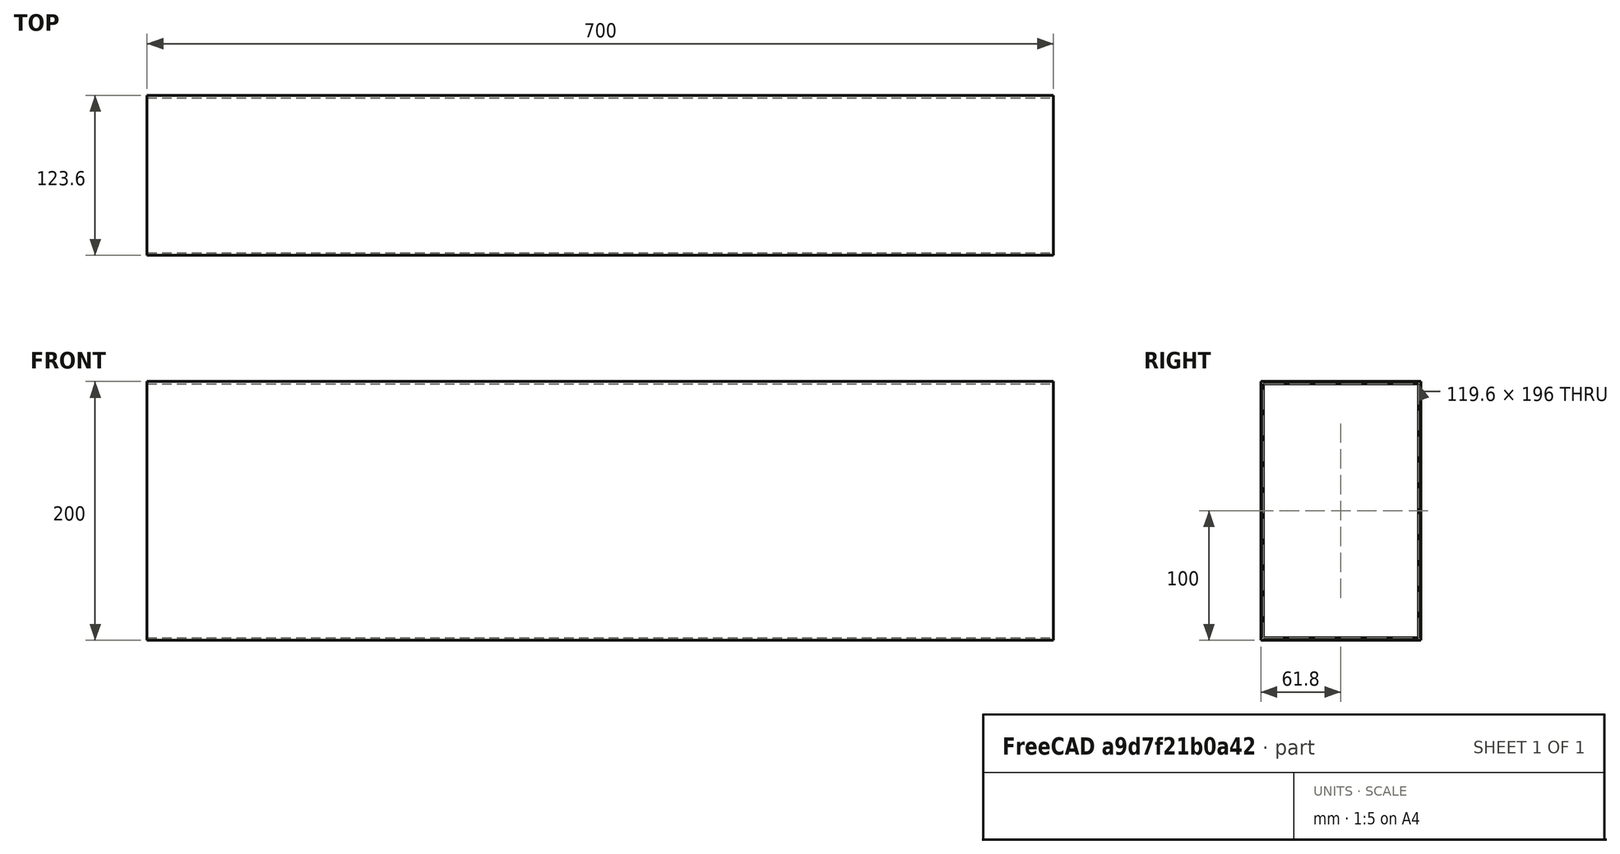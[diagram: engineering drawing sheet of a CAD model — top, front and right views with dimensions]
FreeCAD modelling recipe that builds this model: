
FCSTD DOCUMENT  (FreeCAD 0.20R29410 (Git))
Label: bigSling
License: All rights reserved
LicenseURL: http://en.wikipedia.org/wiki/All_rights_reserved
objects: PartDesign::Body×2, Sketcher::SketchObject×1, PartDesign::Pad×1
note: 5 computed .brp shape members not serialized (recipe doc carries the construction recipe); baked Part::Feature solids carry a one-line shape summary decoded from their .brp

FEATURE [PartDesign::Body] Body
  Origin = -> Origin
FEATURE [Sketcher::SketchObject] Sketch
  FullyConstrained = true
  MapMode = 5
  Placement = pos=(0,0,0) rot=(0.57735,0.57735,0.57735;2.0944rad)
  Support = -> [YZ_Plane001]
  sketch-geometry (8):
    g0: LineSegment StartX=0 StartY=0 StartZ=0 EndX=123.6 EndY=0 EndZ=0
    g1: LineSegment StartX=123.6 StartY=0 StartZ=0 EndX=123.6 EndY=-200 EndZ=0
    g2: LineSegment StartX=123.6 StartY=-200 StartZ=0 EndX=0 EndY=-200 EndZ=0
    g3: LineSegment StartX=0 StartY=-200 StartZ=0 EndX=0 EndY=0 EndZ=0
    g4: LineSegment StartX=2 StartY=-2 StartZ=0 EndX=121.6 EndY=-2 EndZ=0
    g5: LineSegment StartX=121.6 StartY=-2 StartZ=0 EndX=121.6 EndY=-198 EndZ=0
    g6: LineSegment StartX=121.6 StartY=-198 StartZ=0 EndX=2 EndY=-198 EndZ=0
    g7: LineSegment StartX=2 StartY=-198 StartZ=0 EndX=2 EndY=-2 EndZ=0
  constraints (23):
    c: Coincident(g0,g1)
    c: Coincident(g1,g2)
    c: Coincident(g2,g3)
    c: Coincident(g3,g0)
    c: Horizontal(g0)
    c: Horizontal(g2)
    c: Vertical(g1)
    c: Vertical(g3)
    c: Coincident(g0,g-1)
    c: Coincident(g4,g5)
    c: Coincident(g5,g6)
    c: Coincident(g6,g7)
    c: Coincident(g7,g4)
    c: Horizontal(g4)
    c: Horizontal(g6)
    c: Vertical(g5)
    c: Vertical(g7)
    c: DistanceY(g3,g3) = 200
    c: DistanceX(g2,g2) = 123.6
    c: DistanceX(g2,g6) = 2
    c: DistanceY(g4,g0) = 2
    c: DistanceX(g5,g1) = 2
    c: DistanceY(g2,g6) = 2
FEATURE [PartDesign::Pad] Pad
  Direction = (1,-2e-16,3e-16)
  Length = 700
  Length2 = 10
  Placement = pos=(0,0,0) rot=(0.57735,0.57735,0.57735;2.0944rad)
  Profile = -> Sketch
  ReferenceAxis = -> Sketch [N_Axis]
  Type = 0
FEATURE [PartDesign::Body] Body001
  Group = -> [Sketch,Pad]
  Origin = -> Origin001
  Tip = -> Pad
